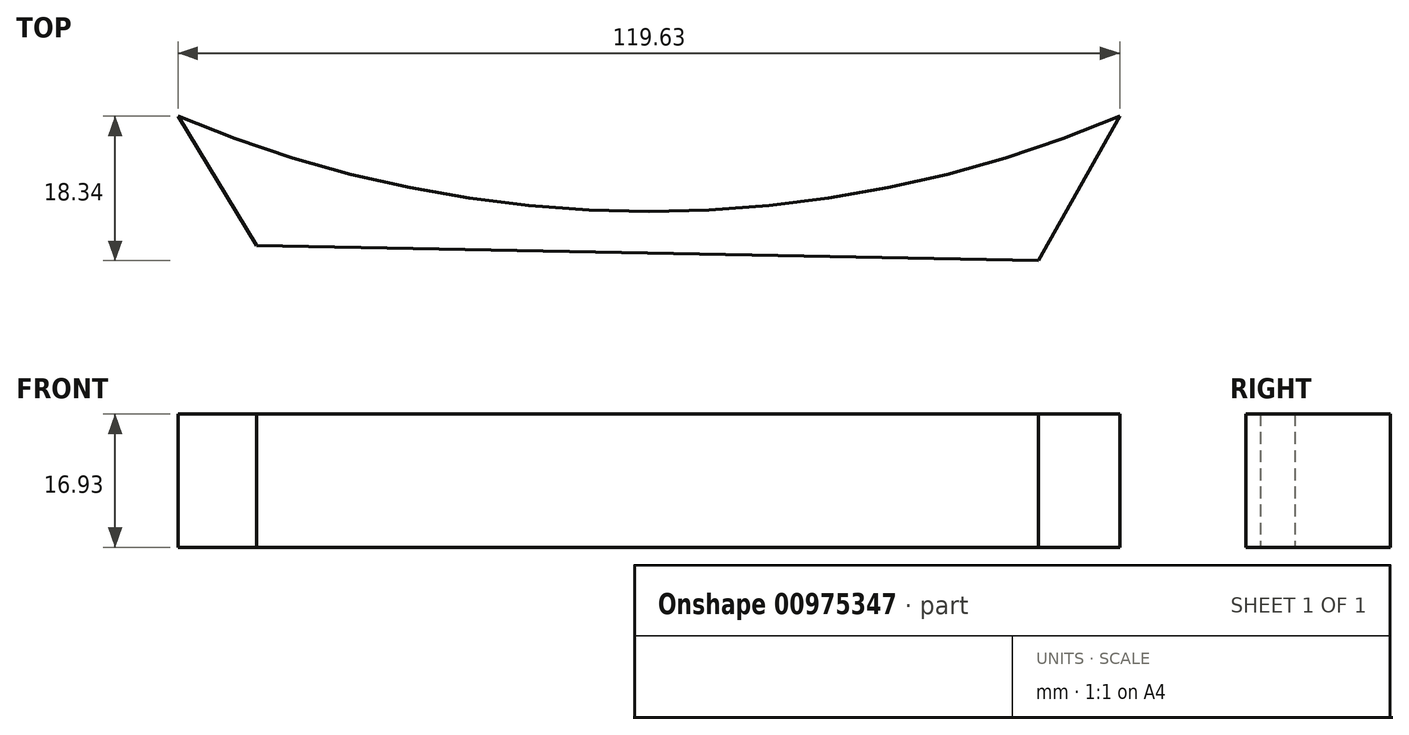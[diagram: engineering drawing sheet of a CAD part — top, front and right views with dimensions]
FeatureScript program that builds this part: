
annotation { "Feature Type Name" : "Feature", "Feature Type Description" : "" }
export const myFeature = defineFeature(function(context is Context, id is Id, definition is map)
    precondition{}
    {
        {
            var Q0;
            Q0=qCreatedBy(makeId("Top.planeOp"),FACE);
            var sketch = newSketch(context, id + "F0", { "sketchPlane" : qUnion([Q0])});
            skArc(sketch, "E0", {"start": v(-60.1, 11.14) * mm, "mid": v(0.93, -1.22) * mm, "end": v(61.97, 11.14) * mm});
            skLineSegment(sketch, "E1", {"start": v(-49.91, -5.65) * mm, "end": v(-60.1, 11.14) * mm});
            skLineSegment(sketch, "E2", {"start": v(51.4, -7.58) * mm, "end": v(61.97, 11.14) * mm});
            skLineSegment(sketch, "E3", {"start": v(-49.91, -5.65) * mm, "end": v(51.4, -7.58) * mm});
            skSolve(sketch);
        }
        {
            var Q0;
            Q0=makeQuery(id+"F0.imprint","IMPRINT",FACE,{"disambiguationData":[TD([[makeQuery(id+"F0.imprint","IMPRINT",EDGE,{"derivedFrom":sQuery(id+"F0.wireOp",EDGE,"E0")}),-1.0]])]});
            extrude(context, id + "F1", {"entities" : qUnion([Q0]), "depth" : 17.27 * mm, "offsetDistance" : 25.4 * mm});
        }
        {
            var Q0;
            Q0=makeQuery(id+"F1.opExtrude","SWEPT_BODY",BODY,{"disambiguationData":[OSD([sQuery(id+"F0.wireOp",EDGE,"E0"),sQuery(id+"F0.wireOp",EDGE,"6ee851bc-aa36-4153-8978-3d2bafaf4182"),sQuery(id+"F0.wireOp",EDGE,"E1"),sQuery(id+"F0.wireOp",EDGE,"E2")])]});
            var Q1;
            Q1=makeQuery(id+"F1.opExtrude","CAP_VERTEX",VERTEX,{"disambiguationData":[OSD([sQuery(id+"F0.wireOp",EDGE,"E0"),sQuery(id+"F0.wireOp",EDGE,"E1")])],"isStart":true});
            transform(context, id + "F2", {"entities" : qUnion([Q0]), "transformType" : TransformType.SCALE_UNIFORMLY, "scale" : .98, "scalePoint" : qUnion([Q1]), "makeCopy" : false});
        }
    });
